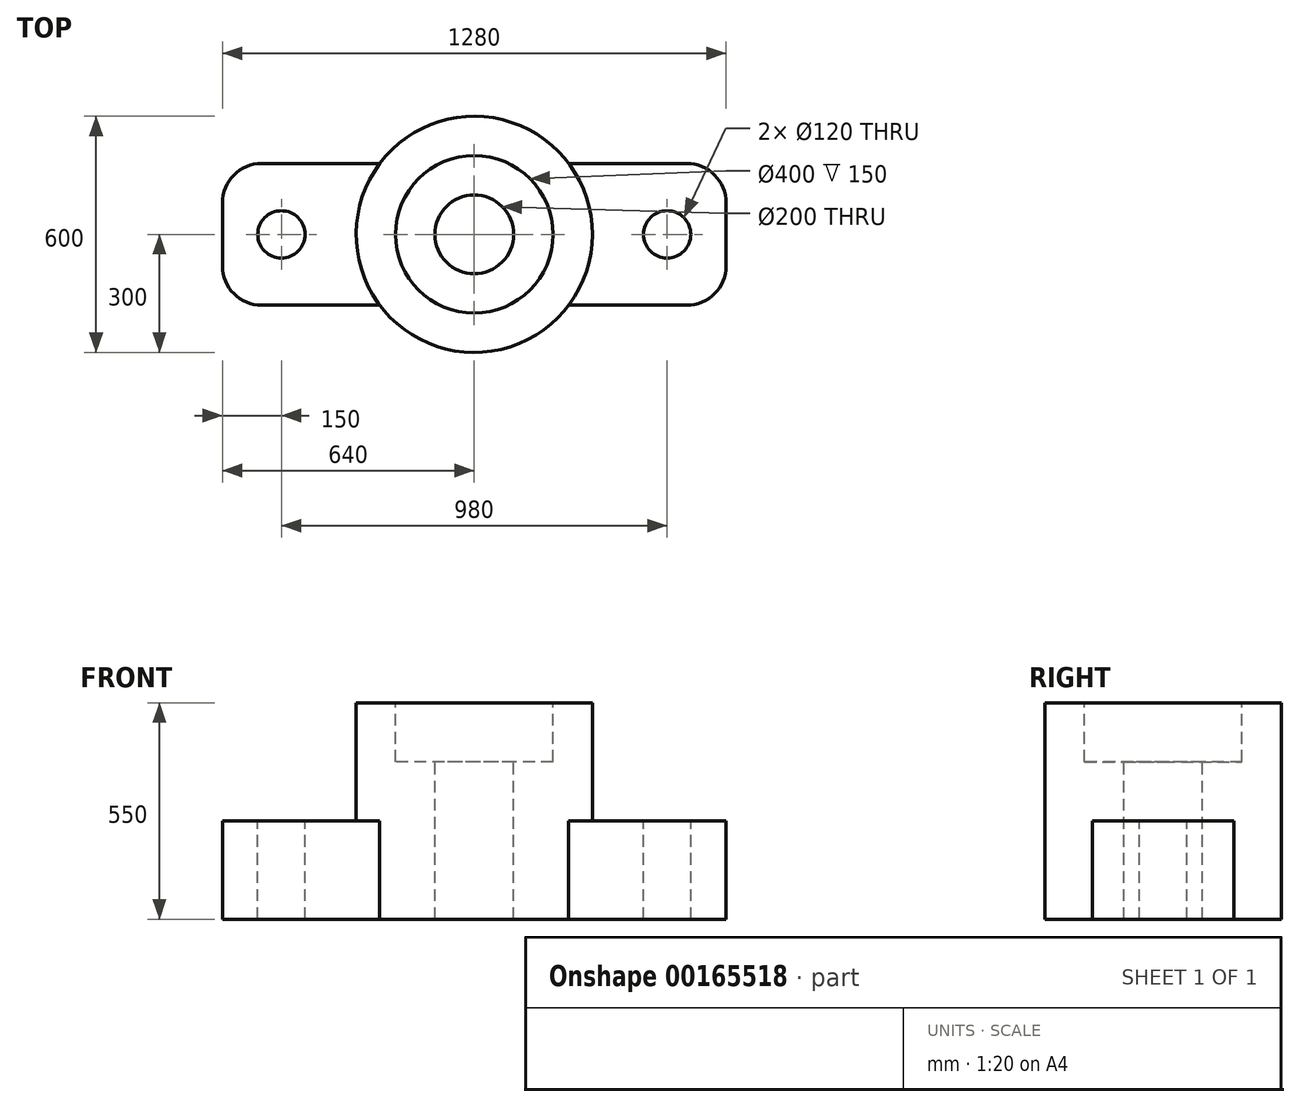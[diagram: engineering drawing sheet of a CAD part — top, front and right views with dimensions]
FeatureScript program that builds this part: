
annotation { "Feature Type Name" : "Feature", "Feature Type Description" : "" }
export const myFeature = defineFeature(function(context is Context, id is Id, definition is map)
    precondition{}
    {
        {
            var Q0;
            Q0=makeQuery(id+"FqGXgp0Uf5qt2j6_0.opExtrude","CAP_FACE",FACE,{"disambiguationData":[OSD([sQuery(id+"FtkUsP9dzIjWhZC_0.wireOp",EDGE,"pFPemjKc-cCHo-l5CX-SveL-TwA0EJSzq2CX")])],"isStart":false});
            var sketch = newSketch(context, id + "F0", { "sketchPlane" : qUnion([Q0])});
            skCircle(sketch, "E0", {"center": v(0, 0) * mm, "radius": 200 * mm});
            skSolve(sketch);
        }
        {
            var Q0;
            Q0=qCreatedBy(makeId("Top.planeOp"),FACE);
            var sketch = newSketch(context, id + "F1", { "sketchPlane" : qUnion([Q0])});
            skCircle(sketch, "E1", {"center": v(0, 0) * mm, "radius": 300 * mm});
            skSolve(sketch);
        }
        {
            var Q0;
            Q0 = qSketchRegion(id + "F1", true);
            extrude(context, id + "F2", {"entities" : qUnion([Q0]), "depth" : 550 * mm});
        }
        {
            var Q0;
            Q0=makeQuery(id+"F2.opExtrude","CAP_FACE",FACE,{"disambiguationData":[OSD([sQuery(id+"F1.wireOp",EDGE,"E1")])],"isStart":false});
            var sketch = newSketch(context, id + "F3", { "sketchPlane" : qUnion([Q0])});
            skCircle(sketch, "E2", {"center": v(0, 0) * mm, "radius": 200 * mm});
            skSolve(sketch);
        }
        {
            var Q0;
            Q0 = qSketchRegion(id + "F3", true);
            extrude(context, id + "F4", {"entities" : qUnion([Q0]), "operationType" : NewBodyOperationType.REMOVE, "oppositeDirection" : true, "depth" : 150 * mm});
        }
        {
            var Q0;
            Q0=makeQuery(id+"F4.boolean.opBoolean","COPY",FACE,{"derivedFrom":makeQuery(id+"F4.opExtrude","CAP_FACE",FACE,{"disambiguationData":[OSD([sQuery(id+"F3.wireOp",EDGE,"E2")])],"isStart":false})});
            var sketch = newSketch(context, id + "F5", { "sketchPlane" : qUnion([Q0])});
            skCircle(sketch, "E3", {"center": v(0, 0) * mm, "radius": 100 * mm});
            skSolve(sketch);
        }
        {
            var Q0;
            Q0 = qSketchRegion(id + "F5", true);
            extrude(context, id + "F6", {"entities" : qUnion([Q0]), "operationType" : NewBodyOperationType.REMOVE, "endBound" : BoundingType.THROUGH_ALL, "oppositeDirection" : true, "depth" : 25 * mm});
        }
        {
            var Q0;
            Q0=makeQuery(id+"F2.opExtrude","CAP_FACE",FACE,{"disambiguationData":[OSD([sQuery(id+"F1.wireOp",EDGE,"E1")])],"isStart":true});
            var sketch = newSketch(context, id + "F7", { "sketchPlane" : qUnion([Q0])});
            skLineSegment(sketch, "E4.bottom", {"start": v(-240, 180) * mm, "end": v(-540, 180) * mm});
            skLineSegment(sketch, "E4.top", {"start": v(-240, -180) * mm, "end": v(-540, -180) * mm});
            skLineSegment(sketch, "E4.left", {"start": v(-240, 180) * mm, "end": v(-240, -180) * mm});
            skLineSegment(sketch, "E4.right", {"start": v(-640, 80) * mm, "end": v(-640, -80) * mm});
            skPoint(sketch, "E5", {"position": v(-300, 0) * mm});
            skPoint(sketch, "E6.visualSharp", {"position": v(-640, -180) * mm});
            skArc(sketch, "E6.filletArc", {"start": v(-640, -80) * mm, "mid": v(-610.71, -150.71) * mm, "end": v(-540, -180) * mm});
            skPoint(sketch, "E7.visualSharp", {"position": v(-640, 180) * mm});
            skArc(sketch, "E7.filletArc", {"start": v(-540, 180) * mm, "mid": v(-610.71, 150.71) * mm, "end": v(-640, 80) * mm});
            skSolve(sketch);
        }
        {
            var Q0;
            Q0 = qSketchRegion(id + "F7", true);
            extrude(context, id + "F8", {"entities" : qUnion([Q0]), "operationType" : NewBodyOperationType.ADD, "oppositeDirection" : true, "depth" : 250 * mm});
        }
        {
            var Q0;
            Q0=makeQuery(id+"F8.boolean.opBoolean","MERGE",FACE,{"derivedFrom":[makeQuery(id+"F2.opExtrude","CAP_FACE",FACE,{"disambiguationData":[OSD([sQuery(id+"F1.wireOp",EDGE,"E1")])],"isStart":true}),makeQuery(id+"F8.opExtrude","CAP_FACE",FACE,{"disambiguationData":[OSD([sQuery(id+"F7.wireOp",EDGE,"E4.bottom"),sQuery(id+"F7.wireOp",EDGE,"E4.top"),sQuery(id+"F7.wireOp",EDGE,"E4.left"),sQuery(id+"F7.wireOp",EDGE,"E4.right"),sQuery(id+"F7.wireOp",EDGE,"E6.filletArc"),sQuery(id+"F7.wireOp",EDGE,"E7.filletArc")])],"isStart":true})]});
            var sketch = newSketch(context, id + "F9", { "sketchPlane" : qUnion([Q0])});
            skLineSegment(sketch, "E8.bottom", {"start": v(240, 180) * mm, "end": v(540, 180) * mm});
            skLineSegment(sketch, "E8.top", {"start": v(240, -180) * mm, "end": v(540, -180) * mm});
            skLineSegment(sketch, "E8.left", {"start": v(240, 180) * mm, "end": v(240, -180) * mm});
            skLineSegment(sketch, "E8.right", {"start": v(640, 80) * mm, "end": v(640, -80) * mm});
            skPoint(sketch, "E9", {"position": v(300, 0) * mm});
            skPoint(sketch, "E10.visualSharp", {"position": v(640, -180) * mm});
            skArc(sketch, "E10.filletArc", {"start": v(540, -180) * mm, "mid": v(610.71, -150.71) * mm, "end": v(640, -80) * mm});
            skPoint(sketch, "E11.visualSharp", {"position": v(640, 180) * mm});
            skArc(sketch, "E11.filletArc", {"start": v(640, 80) * mm, "mid": v(610.71, 150.71) * mm, "end": v(540, 180) * mm});
            skSolve(sketch);
        }
        {
            var Q0;
            Q0 = qSketchRegion(id + "F9", true);
            extrude(context, id + "F10", {"entities" : qUnion([Q0]), "operationType" : NewBodyOperationType.ADD, "oppositeDirection" : true, "depth" : 250 * mm});
        }
        {
            var Q0;
            Q0=makeQuery(id+"F10.opExtrude","CAP_FACE",FACE,{"disambiguationData":[OSD([sQuery(id+"F9.wireOp",EDGE,"E8.bottom"),sQuery(id+"F9.wireOp",EDGE,"E8.top"),sQuery(id+"F9.wireOp",EDGE,"E8.left"),sQuery(id+"F9.wireOp",EDGE,"E8.right"),sQuery(id+"F9.wireOp",EDGE,"E10.filletArc"),sQuery(id+"F9.wireOp",EDGE,"E11.filletArc")])],"isStart":false});
            var sketch = newSketch(context, id + "F11", { "sketchPlane" : qUnion([Q0])});
            skCircle(sketch, "E12", {"center": v(490, 0) * mm, "radius": 60 * mm});
            skLineSegment(sketch, "E13", {"start": v(640, 0) * mm, "end": v(300, 0) * mm});
            skSolve(sketch);
        }
        {
            var Q0;
            Q0 = qSketchRegion(id + "F11", true);
            extrude(context, id + "F12", {"entities" : qUnion([Q0]), "operationType" : NewBodyOperationType.REMOVE, "endBound" : BoundingType.THROUGH_ALL, "oppositeDirection" : true, "depth" : 25 * mm});
        }
        {
            var Q0;
            Q0=makeQuery(id+"F8.opExtrude","CAP_FACE",FACE,{"disambiguationData":[OSD([sQuery(id+"F7.wireOp",EDGE,"E4.bottom"),sQuery(id+"F7.wireOp",EDGE,"E4.top"),sQuery(id+"F7.wireOp",EDGE,"E4.left"),sQuery(id+"F7.wireOp",EDGE,"E4.right"),sQuery(id+"F7.wireOp",EDGE,"E6.filletArc"),sQuery(id+"F7.wireOp",EDGE,"E7.filletArc")])],"isStart":false});
            var sketch = newSketch(context, id + "F13", { "sketchPlane" : qUnion([Q0])});
            skCircle(sketch, "E14", {"center": v(-490, 0) * mm, "radius": 60 * mm});
            skSolve(sketch);
        }
        {
            var Q0;
            Q0 = qSketchRegion(id + "F13", true);
            extrude(context, id + "F14", {"entities" : qUnion([Q0]), "operationType" : NewBodyOperationType.REMOVE, "endBound" : BoundingType.THROUGH_ALL, "oppositeDirection" : true, "depth" : 25 * mm});
        }
    });
